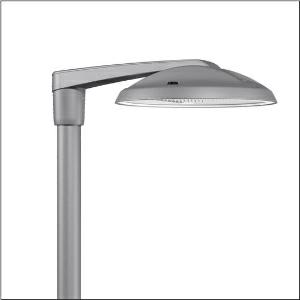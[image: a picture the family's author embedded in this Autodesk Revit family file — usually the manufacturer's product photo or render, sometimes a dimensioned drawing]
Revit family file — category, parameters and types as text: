
# Revit family: dl_r__50_mini___st1_0a_5xa248d33s08le_e5ac
name_source: partatom
category: Lighting Fixtures
units: mm (PartAtom-declared; Revit-internal decimal feet)

## family parameters
Cut with Voids When Loaded = No
Host = Face
Light Source = No
Part Type = Normal
Room Calculation Point = No
Round Connector Dimension = Use Diameter
Shared = No

## types (1)
- --- (1 x LED, 10040 lm, 66.2 W, 3000K)
    Apparent Load = 66 VA
    CIE Flux Codes = 37 72 97 100 100
    Color Rendering = 70
    Color Temperature = 3000K
    Default Elevation = 1800 mm
    Description = DL® 50 mini, mast luminaire, primary light control with lens, of PMMA, primary optical cover: cover, of toughened safety glass, transparent, light distribution: ST1.0a, light emission: direct distribution, primary light characteristic: asymmetric, installation type: post-top, side-entry, LED, High Power LED, rated luminous flux: 10.040lm, luminous efficacy: 152lm/W, light colour: 730, colour temperature: 3000K, control: overheat protection, constant luminous flux control, time-dependent luminous flux control, flexible luminous flux parameterisation, mains connection: 230..240V, AC, 50/60Hz, connection cable pre-assembled, cable length: 8,5m, start of lifetime: 66W, end of service life: 68W, reduction: 32W, luminaire housing, of diecast aluminium, powder-coated, Siteco® metallic grey (DB 702S), inclination adjustable: 0°, 5°, 10° (post-top) | 0°, -5°, -10°, -15° (side-entry), please order mast post-top element or mast side-entry element separately, diameter: 500mm, height: 115mm, post-top: for spigot size d x l = 76 x 100mm; with reducer (optional accessory) 60 x 100mm | side-entry: for spigot size d x l = 60 x 100mm; with reducer (optional accessory) 42 x 100mm, Smart Interface above, protection rating (complete): IP66, insulation class (complete): insulation class II (safety insulation), certification: CE, ENEC, VDE, impact resistance: IK08, permissible operating ambient temperature for outdoor applications: -25..+40°C, standard-compliant lighting for roads and squares, packaging unit: 1 piece

Light Distribution: ST1.0a
    Height = 115 mm
    Lamp = 1 x LED
    Lamp Light Flux = 10040 lm
    Lamp Power = 66.2 W
    Lamp count = 1
    Length = 500 mm
    Luminous efficacy = 152 lm/W
    Manufacturer = Siteco
    ModVariant = No
    Model = 5XA248D33S08LE
    Number of Poles = 1
    OnlyDefault = Yes
    Power Factor = 1
    Product Name = DL® 50 mini | ST1.0a
    Product group = mast luminaire | pylon top
    ProductGroupID = 6100
    Protection Class = Protection class II
    Protection Degree = IP 66
    RLX_Detail_Level = 1
    RLX_Emergency_Light_Flux = 0 lm
    RLX_Emergency_Type = 0
    RLX_Emergency_Type_DB = No
    RlxData = <blob elided: 105961 chars, md5=8ea63b17>
    Socket = socket
    Standby Power = 0 W
    System Light Flux = 10040 lm
    System Power = 66 W
    Type Comments = factory setting: luminous flux: 100 % | dim-lin: 254 | 691 mA
    Type Image = l_1251788.jpg
    URL = http://relux.com
    VarID = @adj_023659
    Voltage = 0 V
    Weight = 0.00 kg
    Width = 0 mm  [stored 0 ft]

note: [stored X ft] marks values corroborated as IEEE doubles in the binary element streams (Revit-internal decimal feet)

## geometry (parser evidence)
native form markers: Blend x4, Sweep x11
no freeform markers — native parametric forms only
